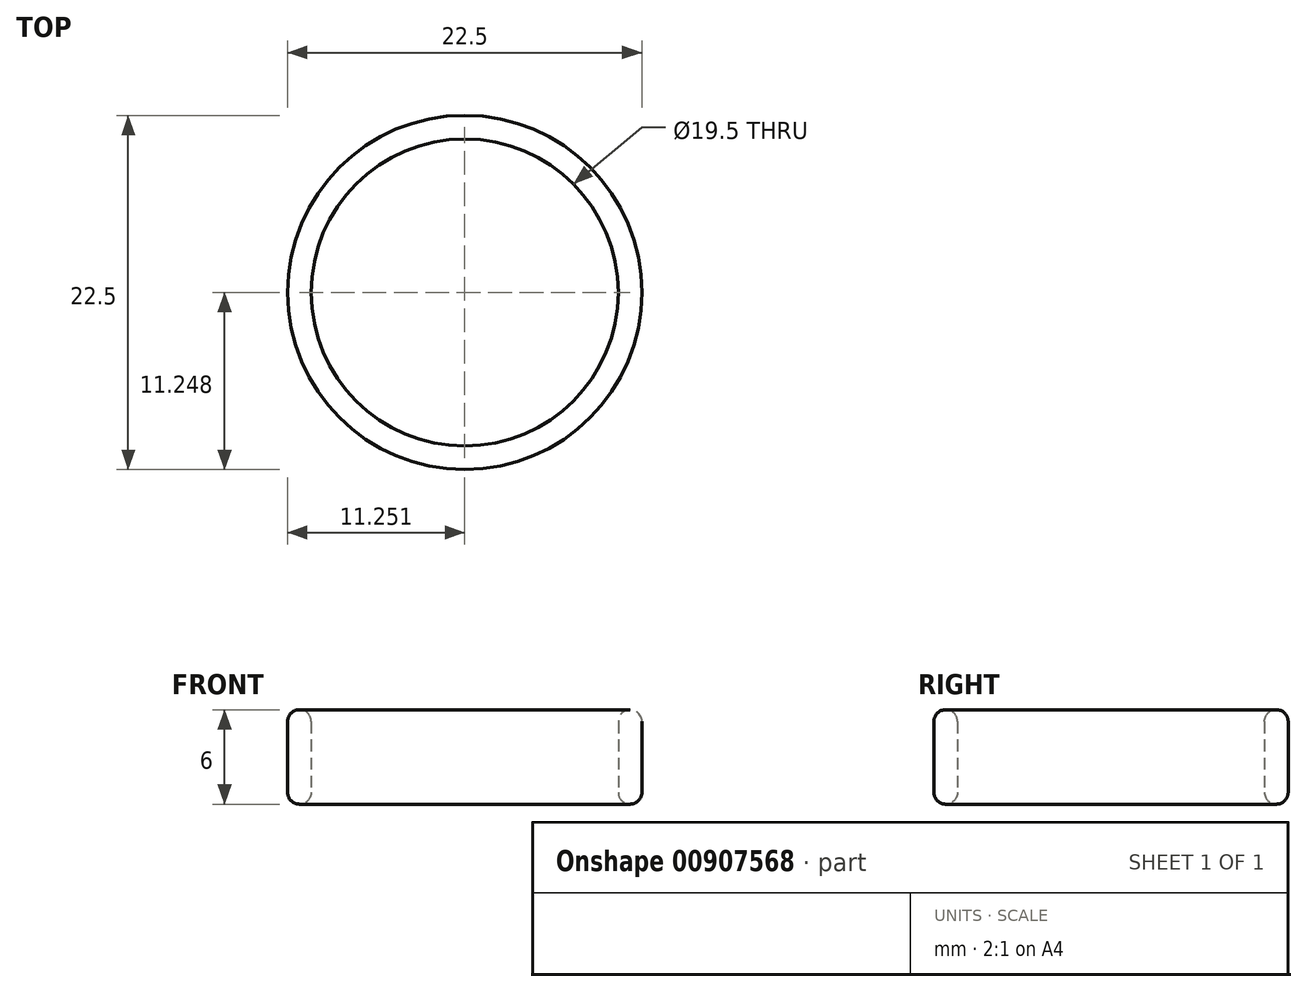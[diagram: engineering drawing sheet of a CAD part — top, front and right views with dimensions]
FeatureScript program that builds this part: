
annotation { "Feature Type Name" : "Feature", "Feature Type Description" : "" }
export const myFeature = defineFeature(function(context is Context, id is Id, definition is map)
    precondition{}
    {
        {
            var Q0;
            Q0=qCreatedBy(makeId("Top.planeOp"),FACE);
            var sketch = newSketch(context, id + "F0", { "sketchPlane" : qUnion([Q0]), "disableImprinting" : false});
            skCircle(sketch, "E0", {"center": v(-31.43, 34.68) * mm, "radius": 9.75 * mm});
            skCircle(sketch, "E1", {"center": v(-31.43, 34.68) * mm, "radius": 11.25 * mm});
            skSolve(sketch);
        }
        {
            var Q0;
            Q0=makeQuery(id+"F0.imprint","IMPRINT",FACE,{"disambiguationData":[TD([[makeQuery(id+"F0.imprint","IMPRINT",EDGE,{"derivedFrom":sQuery(id+"F0.wireOp",EDGE,"E0")}),-1.0]])]});
            extrude(context, id + "F1", {"entities" : qUnion([Q0]), "flatOperationType" : FlatOperationType.REMOVE, "depth" : 6 * mm, "offsetDistance" : 25 * mm, "domain" : OperationDomain.MODEL});
        }
        {
            var Q0;
            Q0=makeQuery(id+"F1.opExtrude","CAP_EDGE",EDGE,{"disambiguationData":[OSD([sQuery(id+"F0.wireOp",EDGE,"E0")])],"isStart":false});
            var Q1;
            Q1=makeQuery(id+"F1.opExtrude","CAP_EDGE",EDGE,{"disambiguationData":[OSD([sQuery(id+"F0.wireOp",EDGE,"E1")])],"isStart":false});
            var Q2;
            Q2=makeQuery(id+"F1.opExtrude","CAP_EDGE",EDGE,{"disambiguationData":[OSD([sQuery(id+"F0.wireOp",EDGE,"E1")])],"isStart":true});
            var Q3;
            Q3=makeQuery(id+"F1.opExtrude","CAP_EDGE",EDGE,{"disambiguationData":[OSD([sQuery(id+"F0.wireOp",EDGE,"E0")])],"isStart":true});
            fillet(context, id + "F2", {"entities" : qUnion([Q0, Q1, Q2, Q3]), "radius" : 0.75 * mm, "tangentPropagation" : true, "allowEdgeOverflow" : false});
        }
    });
